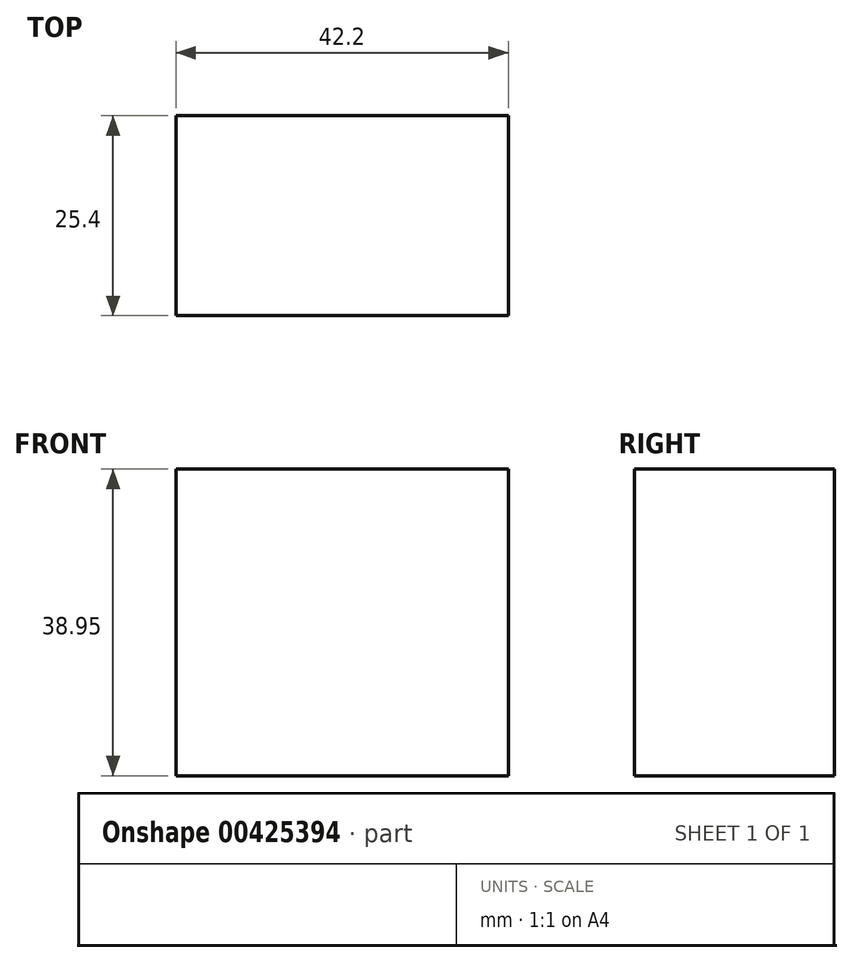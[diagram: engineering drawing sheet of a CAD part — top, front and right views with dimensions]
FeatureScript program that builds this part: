
annotation { "Feature Type Name" : "Feature", "Feature Type Description" : "" }
export const myFeature = defineFeature(function(context is Context, id is Id, definition is map)
    precondition{}
    {
        {
            var Q0;
            Q0=qCreatedBy(makeId("Front.planeOp"),FACE);
            var sketch = newSketch(context, id + "F0", { "sketchPlane" : qUnion([Q0])});
            skLineSegment(sketch, "E0.bottom", {"start": v(-42.2, 38.95) * mm, "end": v(0, 38.95) * mm});
            skLineSegment(sketch, "E0.top", {"start": v(-42.2, 0) * mm, "end": v(0, 0) * mm});
            skLineSegment(sketch, "E0.left", {"start": v(-42.2, 38.95) * mm, "end": v(-42.2, 0) * mm});
            skLineSegment(sketch, "E0.right", {"start": v(0, 38.95) * mm, "end": v(0, 0) * mm});
            skSolve(sketch);
        }
        {
            var Q0;
            Q0=makeQuery(id+"F0.imprint","IMPRINT",FACE,{"disambiguationData":[TD([[makeQuery(id+"F0.imprint","IMPRINT",EDGE,{"derivedFrom":sQuery(id+"F0.wireOp",EDGE,"E0.bottom")}),-1.0]])]});
            extrude(context, id + "F1", {"entities" : qUnion([Q0]), "depth" : 25.4 * mm});
        }
    });
